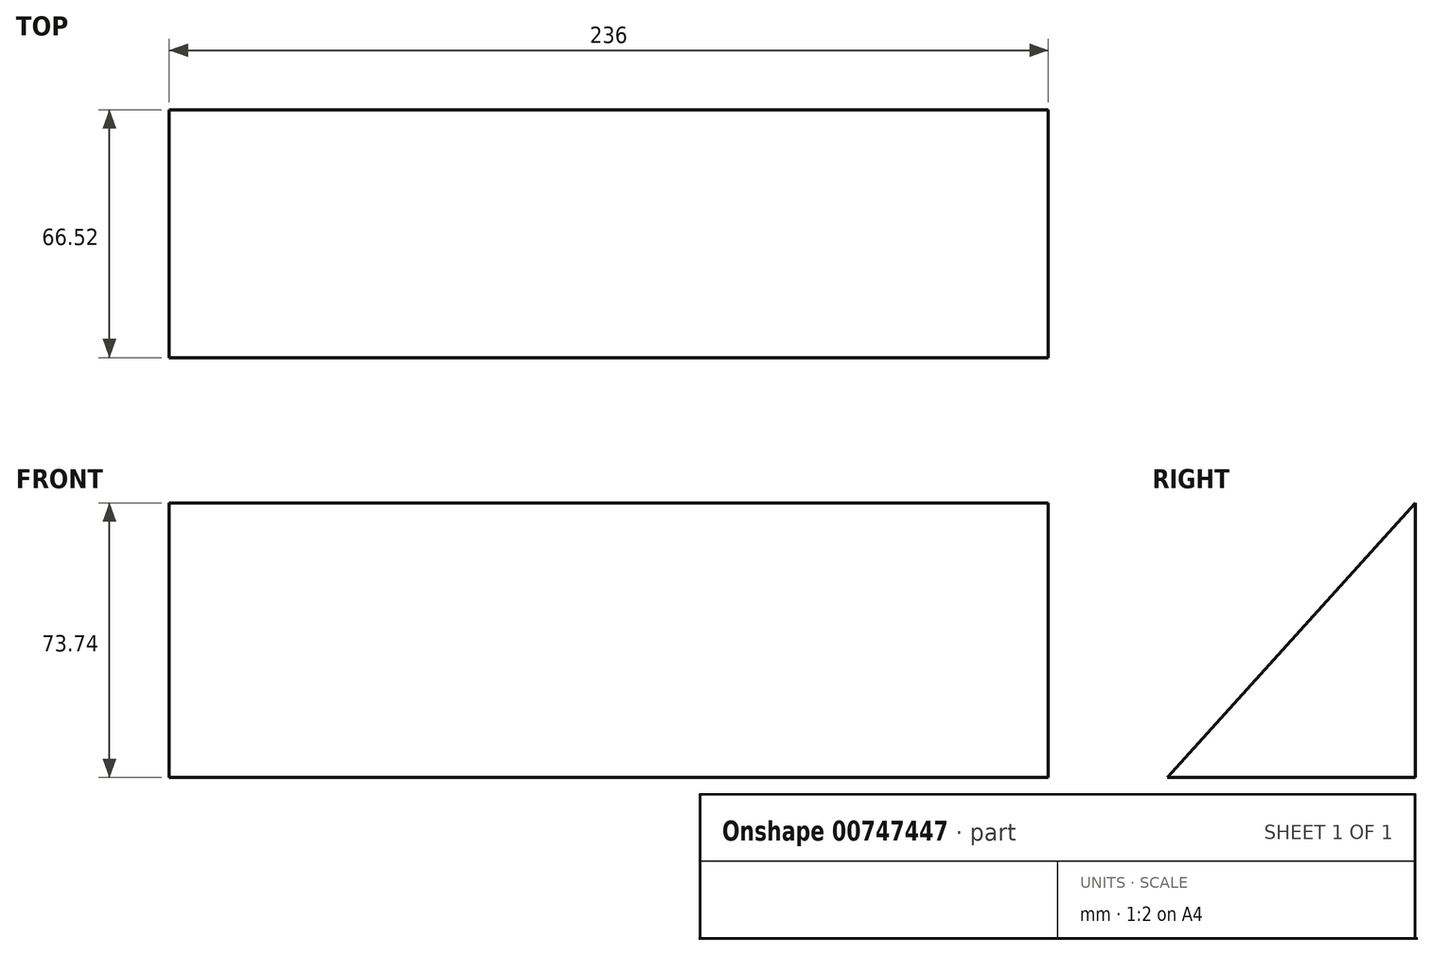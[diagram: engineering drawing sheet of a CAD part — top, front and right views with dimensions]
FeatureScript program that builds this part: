
annotation { "Feature Type Name" : "Feature", "Feature Type Description" : "" }
export const myFeature = defineFeature(function(context is Context, id is Id, definition is map)
    precondition{}
    {
        {
            var Q0;
            Q0=qCreatedBy(makeId("Right.planeOp"),FACE);
            var sketch = newSketch(context, id + "F0", { "sketchPlane" : qUnion([Q0])});
            skLineSegment(sketch, "E0", {"start": v(0, 0) * mm, "end": v(66.52, 73.74) * mm});
            skLineSegment(sketch, "E1", {"start": v(66.52, 73.74) * mm, "end": v(66.52, 0) * mm});
            skLineSegment(sketch, "E2", {"start": v(66.52, 0) * mm, "end": v(0, 0) * mm});
            skSolve(sketch);
        }
        {
            var Q0;
            Q0 = qSketchRegion(id + "F0", true);
            extrude(context, id + "F1", {"entities" : qUnion([Q0]), "depth" : 236 * mm, "offsetDistance" : 25.4 * mm});
        }
    });
